# Revit family: 6438 Post Table
name_source: partatom
category: Furniture
revit_build: Autodesk Revit 2017 (Build: 20171027_0315(x64)
units: mm (PartAtom-declared; Revit-internal decimal feet)

## family parameters
Always vertical = Yes
Cut with Voids When Loaded = No
OmniClass Number = 23.40.20.00
OmniClass Title = General Furniture and Specialties
Room Calculation Point = No
Shared = No
Work Plane-Based = No

## types (1)
- 6438 Post Table
    Description = With its long rectangular table top and sturdy cylindrical legs, the Post Table is the perfect merging of functionality, simplicity and serenity in a classic design expressed with modern minimalism. The structural frame is exceptionally crafted in solid wood, teamed with a table top available in wood veneer. Enjoy loads of leg room in the wide space between the legs on either end, adding to the appeal of this practical, tactile table for dining or meeting in a residential, corporate or hospitality setting.
    Design year = 2019
    Frame = FF Oak Soap horizontal
    Height = 73 cm
    Item No. = 6438
    Legs = FF Oak Soap vertical
    Length = 225 cm
    Manufacturer = Fredericia Furniture
    Model = Post Table
    Table Top = FF Oak Soap horizontal
    URL = https://www.fredericia.com
    Variation Frame - Extra charge = Available in other kinds of wood
    Variation Frame - Standard = Available in other kinds of wood
    Width = 100 cm

## geometry (parser evidence)
native form markers: Sweep x2
no freeform markers — native parametric forms only
